annotation { "Feature Type Name" : "Feature", "Feature Type Description" : "" }
export const myFeature = defineFeature(function(context is Context, id is Id, definition is map)
    precondition{}
    {
        {
            var Q0;
            Q0=qCreatedBy(makeId("Top.planeOp"),FACE);
            var sketch = newSketch(context, id + "F0", { "sketchPlane" : qUnion([Q0])});
            skLineSegment(sketch, "E0", {"start": v(-45, 0) * mm, "end": v(45, 0) * mm, "construction": true});
            skCircle(sketch, "E1", {"center": v(-45, 0) * mm, "radius": 2.5 * mm});
            skCircle(sketch, "E2", {"center": v(45, 0) * mm, "radius": 2.5 * mm});
            skLineSegment(sketch, "E3", {"start": v(-55, 0) * mm, "end": v(-55, 9) * mm});
            skLineSegment(sketch, "E4", {"start": v(-50, 14) * mm, "end": v(-40, 14) * mm});
            skLineSegment(sketch, "E5", {"start": v(-35, 9) * mm, "end": v(-35, 7) * mm});
            skLineSegment(sketch, "E6", {"start": v(-35, 7) * mm, "end": v(35, 7) * mm});
            skLineSegment(sketch, "E7", {"start": v(35, 7) * mm, "end": v(35, 9) * mm});
            skLineSegment(sketch, "E8", {"start": v(40, 14) * mm, "end": v(50, 14) * mm});
            skLineSegment(sketch, "E9.MirrorCS", {"start": v(-55, 0) * mm, "end": v(-55, -9) * mm});
            skLineSegment(sketch, "E10.MirrorCS", {"start": v(-50, -14) * mm, "end": v(-40, -14) * mm});
            skLineSegment(sketch, "E11.MirrorCS", {"start": v(-35, -9) * mm, "end": v(-35, -7) * mm});
            skLineSegment(sketch, "E12.MirrorCS", {"start": v(-35, -7) * mm, "end": v(35, -7) * mm});
            skLineSegment(sketch, "E13.MirrorCS", {"start": v(35, -7) * mm, "end": v(35, -9) * mm});
            skLineSegment(sketch, "E14.MirrorCS", {"start": v(40, -14) * mm, "end": v(50, -14) * mm});
            skLineSegment(sketch, "E15", {"start": v(55, 9) * mm, "end": v(55, -9) * mm});
            skPoint(sketch, "E16.visualSharp", {"position": v(-55, 14) * mm});
            skArc(sketch, "E16.filletArc", {"start": v(-50, 14) * mm, "mid": v(-53.54, 12.54) * mm, "end": v(-55, 9) * mm});
            skPoint(sketch, "E17.visualSharp", {"position": v(-55, -14) * mm});
            skArc(sketch, "E17.filletArc", {"start": v(-55, -9) * mm, "mid": v(-53.54, -12.54) * mm, "end": v(-50, -14) * mm});
            skPoint(sketch, "E18.visualSharp", {"position": v(-35, -14) * mm});
            skArc(sketch, "E18.filletArc", {"start": v(-40, -14) * mm, "mid": v(-36.46, -12.54) * mm, "end": v(-35, -9) * mm});
            skPoint(sketch, "E19.visualSharp", {"position": v(-35, 14) * mm});
            skArc(sketch, "E19.filletArc", {"start": v(-35, 9) * mm, "mid": v(-36.46, 12.54) * mm, "end": v(-40, 14) * mm});
            skPoint(sketch, "E20.visualSharp", {"position": v(35, 14) * mm});
            skArc(sketch, "E20.filletArc", {"start": v(40, 14) * mm, "mid": v(36.46, 12.54) * mm, "end": v(35, 9) * mm});
            skPoint(sketch, "E21.visualSharp", {"position": v(55, 14) * mm});
            skArc(sketch, "E21.filletArc", {"start": v(55, 9) * mm, "mid": v(53.54, 12.54) * mm, "end": v(50, 14) * mm});
            skPoint(sketch, "E22.visualSharp", {"position": v(55, -14) * mm});
            skArc(sketch, "E22.filletArc", {"start": v(50, -14) * mm, "mid": v(53.54, -12.54) * mm, "end": v(55, -9) * mm});
            skPoint(sketch, "E23.visualSharp", {"position": v(35, -14) * mm});
            skArc(sketch, "E23.filletArc", {"start": v(35, -9) * mm, "mid": v(36.46, -12.54) * mm, "end": v(40, -14) * mm});
            skSolve(sketch);
        }
        {
            var Q0;
            Q0=makeQuery(id+"F0.imprint","IMPRINT",FACE,{"disambiguationData":[TD([[makeQuery(id+"F0.imprint","IMPRINT",EDGE,{"derivedFrom":sQuery(id+"F0.wireOp",EDGE,"E1")}),-1.0]])]});
            extrude(context, id + "F1", {"entities" : qUnion([Q0]), "oppositeDirection" : true, "depth" : 4 * mm});
        }
        {
            var Q0;
            Q0=qCreatedBy(makeId("Top.planeOp"),FACE);
            var sketch = newSketch(context, id + "F2", { "sketchPlane" : qUnion([Q0])});
            skText(sketch, "E24", { "text": "HAN", "fontName": "OpenSans-BoldItalic.ttf"});
            const initialGuessF2  = {"E24": [-0.03386, 0, 1, 0, 0.00526]};
            skSetInitialGuess(sketch, initialGuessF2);
            skSolve(sketch);
        }
        {
            var Q0;
            Q0 = qSketchRegion(id + "F2", true);
            extrude(context, id + "F3", {"entities" : qUnion([Q0]), "operationType" : NewBodyOperationType.REMOVE, "oppositeDirection" : true, "depth" : 5 * mm});
        }
        {
            var Q0;
            Q0=qCreatedBy(makeId("Top.planeOp"),FACE);
            var sketch = newSketch(context, id + "F4", { "sketchPlane" : qUnion([Q0])});
            skText(sketch, "E25", { "text": "Built Environment", "fontName": "OpenSans-BoldItalic.ttf"});
            const initialGuessF4  = {"E25": [-0.03362, -0.00615, 1, 0, 0.0048]};
            skSetInitialGuess(sketch, initialGuessF4);
            skSolve(sketch);
        }
        {
            var Q0;
            Q0 = qSketchRegion(id + "F4", true);
            extrude(context, id + "F5", {"entities" : qUnion([Q0]), "operationType" : NewBodyOperationType.REMOVE, "oppositeDirection" : true, "depth" : 5 * mm});
        }
    });